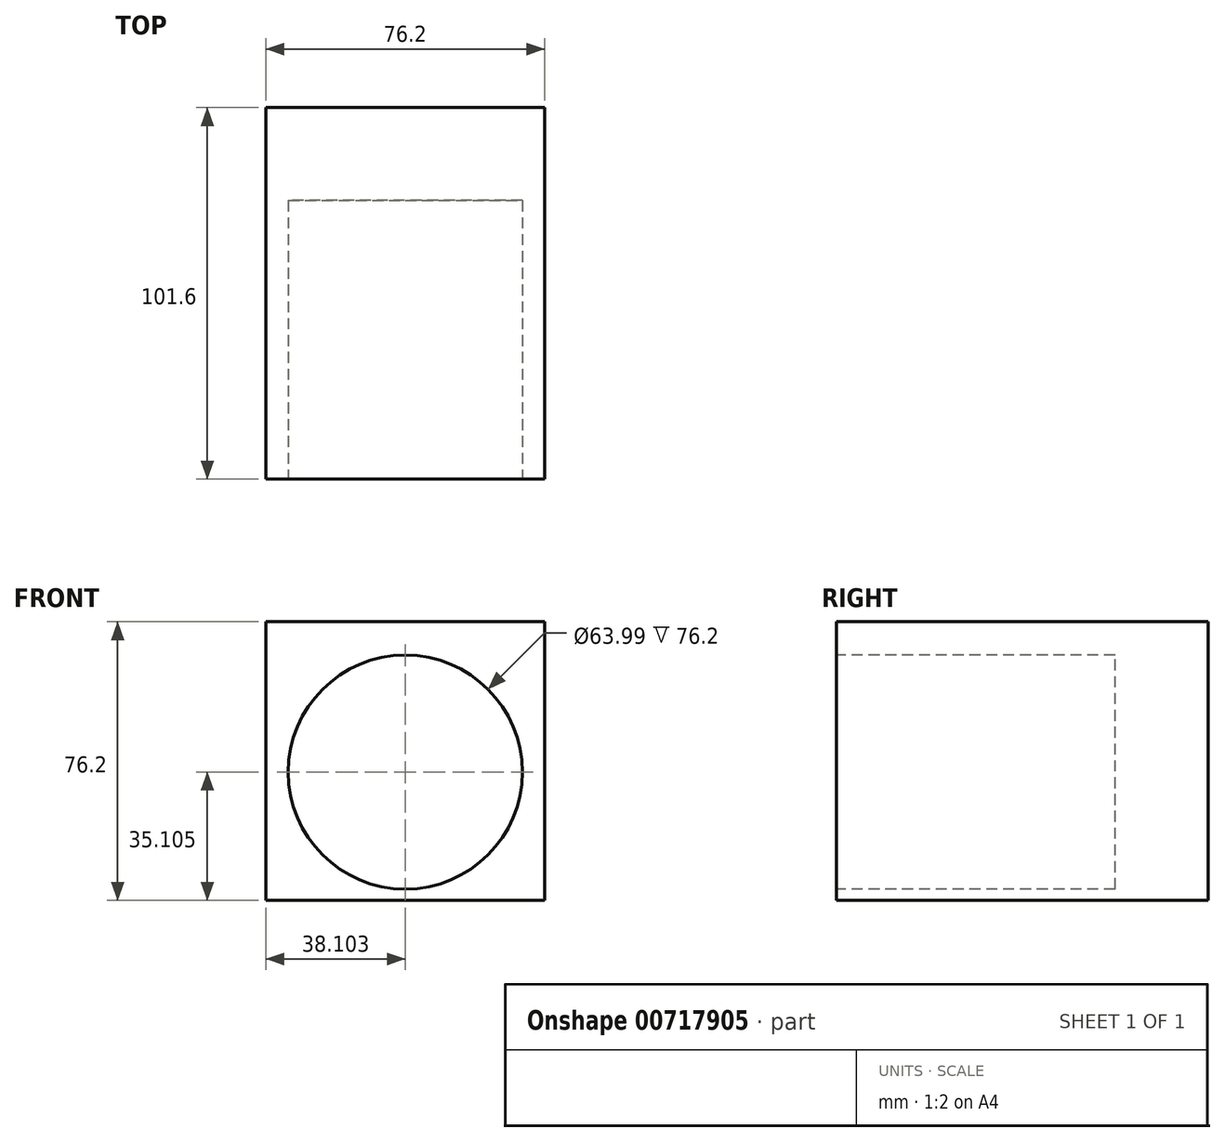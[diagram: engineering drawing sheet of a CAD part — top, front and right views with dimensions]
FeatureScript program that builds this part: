
annotation { "Feature Type Name" : "Feature", "Feature Type Description" : "" }
export const myFeature = defineFeature(function(context is Context, id is Id, definition is map)
    precondition{}
    {
        {
            var Q0;
            Q0=qCreatedBy(makeId("Front.planeOp"),FACE);
            var sketch = newSketch(context, id + "F0", { "sketchPlane" : qUnion([Q0])});
            skLineSegment(sketch, "E0.bottom", {"start": v(-5.77, 8.33) * mm, "end": v(70.43, 8.33) * mm});
            skLineSegment(sketch, "E0.top", {"start": v(-5.77, -67.87) * mm, "end": v(70.43, -67.87) * mm});
            skLineSegment(sketch, "E0.left", {"start": v(-5.77, 8.33) * mm, "end": v(-5.77, -67.87) * mm});
            skLineSegment(sketch, "E0.right", {"start": v(70.43, 8.33) * mm, "end": v(70.43, -67.87) * mm});
            skSolve(sketch);
        }
        {
            var Q0;
            Q0=makeQuery(id+"F0.imprint","IMPRINT",FACE,{"disambiguationData":[TD([[makeQuery(id+"F0.imprint","IMPRINT",EDGE,{"derivedFrom":sQuery(id+"F0.wireOp",EDGE,"E0.bottom")}),-1.0]])]});
            extrude(context, id + "F1", {"entities" : qUnion([Q0]), "endBound" : BoundingType.SYMMETRIC, "depth" : 101.6 * mm, "offsetDistance" : 25.4 * mm});
        }
        {
            var Q0;
            Q0=makeQuery(id+"F1.opExtrude","CAP_FACE",FACE,{"disambiguationData":[OSD([sQuery(id+"F0.wireOp",EDGE,"E0.bottom"),sQuery(id+"F0.wireOp",EDGE,"E0.top"),sQuery(id+"F0.wireOp",EDGE,"E0.left"),sQuery(id+"F0.wireOp",EDGE,"E0.right")])],"isStart":false});
            var sketch = newSketch(context, id + "F2", { "sketchPlane" : qUnion([Q0])});
            skCircle(sketch, "E1", {"center": v(32.33, -32.76) * mm, "radius": 32 * mm});
            skPoint(sketch, "E1.centerSnap0", {"position": v(32.33, -67.87) * mm});
            skSolve(sketch);
        }
        {
            var Q0;
            Q0=makeQuery(id+"F2.imprint","IMPRINT",FACE,{"disambiguationData":[TD([[makeQuery(id+"F2.imprint","IMPRINT",EDGE,{"derivedFrom":sQuery(id+"F2.wireOp",EDGE,"E1")}),1.0]])]});
            extrude(context, id + "F3", {"entities" : qUnion([Q0]), "operationType" : NewBodyOperationType.REMOVE, "oppositeDirection" : true, "depth" : 76.2 * mm, "offsetDistance" : 25.4 * mm});
        }
    });
